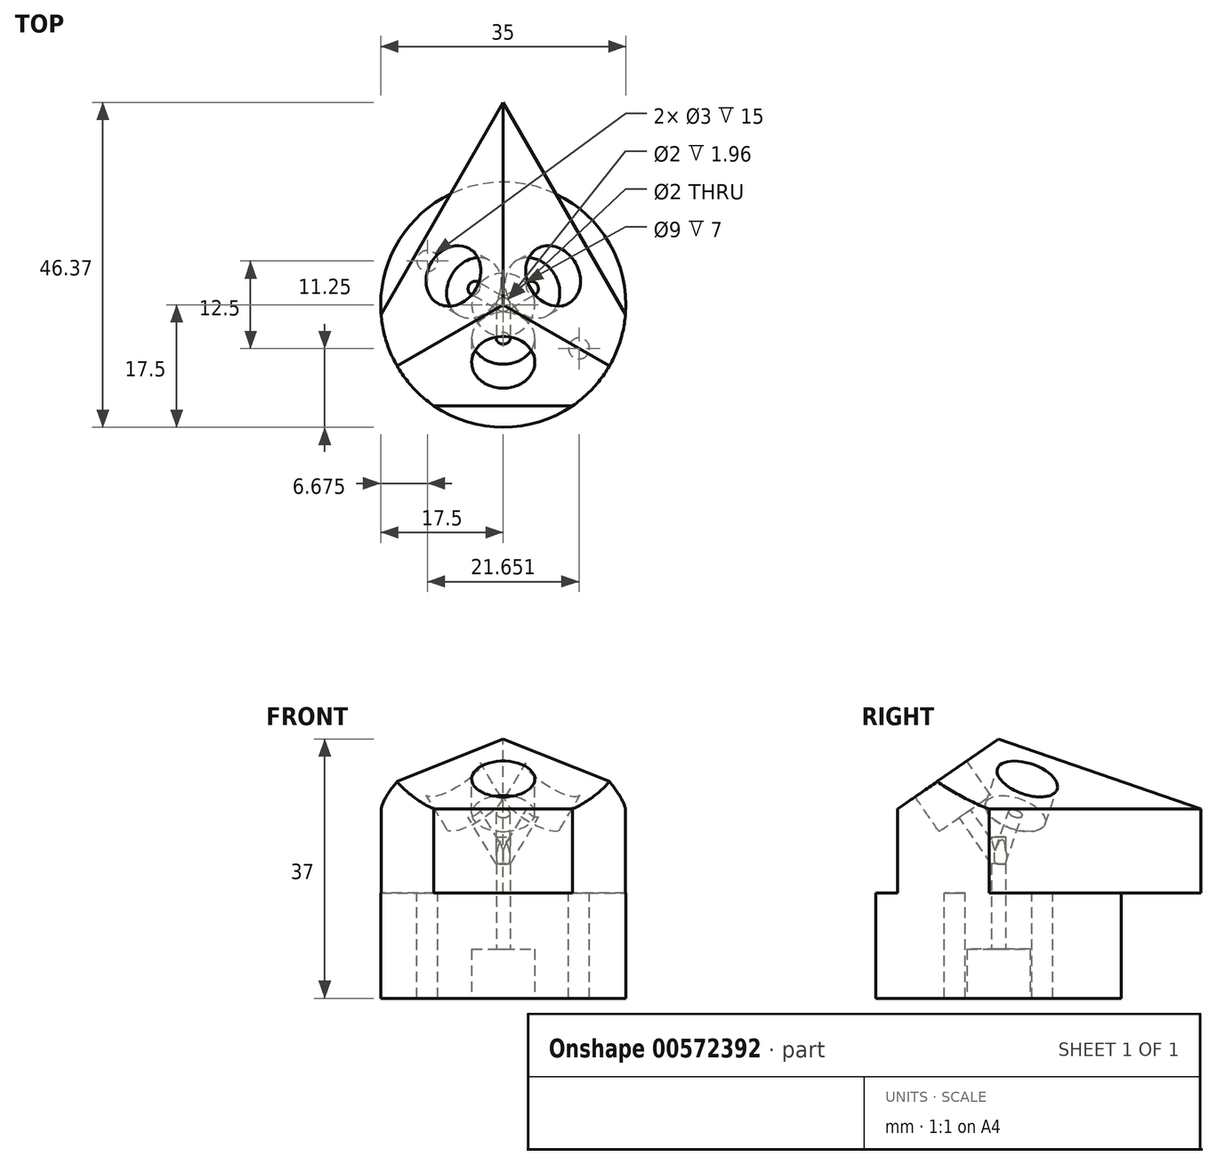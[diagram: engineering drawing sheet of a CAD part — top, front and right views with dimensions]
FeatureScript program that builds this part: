
annotation { "Feature Type Name" : "Feature", "Feature Type Description" : "" }
export const myFeature = defineFeature(function(context is Context, id is Id, definition is map)
    precondition{}
    {
        {
            assignVariable(context, id + "F0", {"name" : "BaseHeight", "anyValue" : 12});
        }
        {
            assignVariable(context, id + "F1", {"name" : "BarbDepth", "anyValue" : 6});
        }
        {
            var Q0;
            Q0=qCreatedBy(makeId("Top.planeOp"),FACE);
            var sketch = newSketch(context, id + "F2", { "sketchPlane" : qUnion([Q0])});
            skLineSegment(sketch, "E0", {"start": v(0, 28.87) * mm, "end": v(-25, -14.43) * mm});
            skLineSegment(sketch, "E1", {"start": v(-25, -14.43) * mm, "end": v(25, -14.43) * mm});
            skLineSegment(sketch, "E2", {"start": v(25, -14.43) * mm, "end": v(0, 28.87) * mm});
            skLineSegment(sketch, "E3", {"start": v(-12.5, 7.22) * mm, "end": v(0, 0) * mm, "construction": true});
            skLineSegment(sketch, "E4", {"start": v(0, 0) * mm, "end": v(0, -14.43) * mm, "construction": true});
            skLineSegment(sketch, "E5", {"start": v(0, 0) * mm, "end": v(12.5, 7.22) * mm, "construction": true});
            skSolve(sketch);
        }
        {
            var Q0;
            Q0=makeQuery(id+"F2.imprint","IMPRINT",FACE,{"disambiguationData":[TD([[makeQuery(id+"F2.imprint","IMPRINT",EDGE,{"derivedFrom":sQuery(id+"F2.wireOp",EDGE,"E0")}),1.0]])]});
            extrude(context, id + "F3", {"entities" : qUnion([Q0]), "oppositeDirection" : true, "depth" : (getVariable(context, 'BaseHeight')) * mm, "offsetDistance" : 25 * mm});
        }
        {
            var Q0;
            Q0=makeQuery(id+"F3.opExtrude","CAP_FACE",FACE,{"disambiguationData":[OSD([sQuery(id+"F2.wireOp",EDGE,"E0"),sQuery(id+"F2.wireOp",EDGE,"E1"),sQuery(id+"F2.wireOp",EDGE,"E2")])],"isStart":true});
            cPlane(context, id + "F4", {"entities" : qUnion([Q0]), "cplaneType" : CPlaneType.OFFSET, "offset" : 10 * mm, "width" : 150 * mm, "height" : 150 * mm});
        }
        {
            var Q0;
            Q0=qCreatedBy(id+"F4.planeOp",FACE);
            var sketch = newSketch(context, id + "F5", { "sketchPlane" : qUnion([Q0])});
            skPoint(sketch, "E6.0", {"position": v(0, 0) * mm});
            skSolve(sketch);
        }
        {
            var Q1;
            Q1=makeQuery(id+"F3.opExtrude","CAP_FACE",FACE,{"disambiguationData":[OSD([sQuery(id+"F2.wireOp",EDGE,"E0"),sQuery(id+"F2.wireOp",EDGE,"E1"),sQuery(id+"F2.wireOp",EDGE,"E2")])],"isStart":true});
            var Q2;
            Q2=sQuery(id+"F5.wireOp",VERTEX,"E6.0");
            loft(context, id + "F6", {"operationType" : NewBodyOperationType.ADD, "sheetProfilesArray" : [{ "sheetProfileEntities" : qUnion([Q1]) }, { "sheetProfileEntities" : qUnion([Q2]) }]});
        }
        {
            var Q0;
            Q0=makeQuery(id+"F3.opExtrude","CAP_FACE",FACE,{"disambiguationData":[OSD([sQuery(id+"F2.wireOp",EDGE,"E0"),sQuery(id+"F2.wireOp",EDGE,"E1"),sQuery(id+"F2.wireOp",EDGE,"E2")])],"isStart":false});
            var sketch = newSketch(context, id + "F7", { "sketchPlane" : qUnion([Q0])});
            skLineSegment(sketch, "E7", {"start": v(12.5, -7.22) * mm, "end": v(0, 0) * mm, "construction": true});
            skLineSegment(sketch, "E8", {"start": v(0, 0) * mm, "end": v(0, 14.43) * mm, "construction": true});
            skLineSegment(sketch, "E9", {"start": v(-12.5, -7.22) * mm, "end": v(0, 0) * mm, "construction": true});
            skSolve(sketch);
        }
        {
            var Q0;
            Q0=makeQuery(id+"F7.imprint","IMPRINT",FACE,{"disambiguationData":[TD([[makeQuery(id+"F7.imprint","IMPRINT",EDGE,{"derivedFrom":makeQuery(id+"F3.opExtrude","CAP_EDGE",EDGE,{"disambiguationData":[OSD([sQuery(id+"F2.wireOp",EDGE,"E0")])],"isStart":false})}),-1.0]])]});
            var sketch = newSketch(context, id + "F8", { "sketchPlane" : qUnion([Q0])});
            skCircle(sketch, "E10", {"center": v(0, 0) * mm, "radius": 1 * mm});
            skSolve(sketch);
        }
        {
            var Q0;
            Q0=makeQuery(id+"F8.imprint","IMPRINT",FACE,{"disambiguationData":[TD([[makeQuery(id+"F8.imprint","IMPRINT",EDGE,{"derivedFrom":sQuery(id+"F8.wireOp",EDGE,"E10")}),1.0]])]});
            extrude(context, id + "F9", {"entities" : qUnion([Q0]), "operationType" : NewBodyOperationType.REMOVE, "oppositeDirection" : true, "depth" : 8 * mm, "offsetDistance" : 25 * mm});
        }
        {
            var Q0;
            Q0=makeQuery(id+"F7.imprint","IMPRINT",FACE,{"disambiguationData":[TD([[makeQuery(id+"F7.imprint","IMPRINT",EDGE,{"derivedFrom":makeQuery(id+"F3.opExtrude","CAP_EDGE",EDGE,{"disambiguationData":[OSD([sQuery(id+"F2.wireOp",EDGE,"E0")])],"isStart":false})}),-1.0]])]});
            var sketch = newSketch(context, id + "F10", { "sketchPlane" : qUnion([Q0])});
            skCircle(sketch, "E11", {"center": v(0, 0) * mm, "radius": 4.5 * mm});
            skSolve(sketch);
        }
        {
            var Q0;
            Q0=makeQuery(id+"F10.imprint","IMPRINT",FACE,{"disambiguationData":[TD([[makeQuery(id+"F10.imprint","IMPRINT",EDGE,{"derivedFrom":sQuery(id+"F10.wireOp",EDGE,"E11")}),1.0]])]});
            extrude(context, id + "F11", {"entities" : qUnion([Q0]), "operationType" : NewBodyOperationType.REMOVE, "oppositeDirection" : true, "depth" : 2 * mm, "offsetDistance" : 25 * mm});
        }
        {
            var Q0;
            {var subQ0=sQuery(id+"F2.wireOp",EDGE,"E1");var subQ1=sQuery(id+"F2.wireOp",EDGE,"E2");var subQ2=sQuery(id+"F2.wireOp",EDGE,"E0");Q0=makeQuery(id+"F6.opLoft","SWEPT_FACE",FACE,{"disambiguationData":[OSD([subQ2,subQ0,subQ1]),TDD([makeQuery(id+"F3.opExtrude","CAP_VERTEX",VERTEX,{"disambiguationData":[OSD([subQ2,subQ0])],"isStart":true}),makeQuery(id+"F3.opExtrude","CAP_VERTEX",VERTEX,{"disambiguationData":[OSD([subQ0,subQ1])],"isStart":true}),makeQuery(id+"F3.opExtrude","CAP_EDGE",EDGE,{"disambiguationData":[OSD([subQ0])],"isStart":true})])]});}
            var sketch = newSketch(context, id + "F12", { "sketchPlane" : qUnion([Q0])});
            skPoint(sketch, "E12.endSnap0", {"position": v(0, -11.86) * mm});
            skLineSegment(sketch, "E13", {"start": v(-12.5, -3.08) * mm, "end": v(0, -4.3) * mm, "construction": true});
            skLineSegment(sketch, "E14", {"start": v(0, -4.3) * mm, "end": v(0, -11.86) * mm, "construction": true});
            skLineSegment(sketch, "E15", {"start": v(12.5, -3.08) * mm, "end": v(0, -4.3) * mm, "construction": true});
            skCircle(sketch, "E16", {"center": v(0, -4.3) * mm, "radius": 1 * mm});
            skCircle(sketch, "E17", {"center": v(0, -4.3) * mm, "radius": 4.5 * mm});
            skLineSegment(sketch, "E18", {"start": v(0, 5.7) * mm, "end": v(0, -4.3) * mm, "construction": true});
            skSolve(sketch);
        }
        {
            var Q0;
            Q0=makeQuery(id+"F12.imprint","IMPRINT",FACE,{"disambiguationData":[TD([[makeQuery(id+"F12.imprint","IMPRINT",EDGE,{"derivedFrom":sQuery(id+"F12.wireOp",EDGE,"E16")}),1.0]])]});
            var Q1;
            Q1=makeQuery(id+"F9.boolean.opBoolean","COPY",FACE,{"derivedFrom":makeQuery(id+"F9.opExtrude","SWEPT_FACE",FACE,{"disambiguationData":[OSD([sQuery(id+"F8.wireOp",EDGE,"E10")])]})});
            extrude(context, id + "F13", {"entities" : qUnion([Q0]), "operationType" : NewBodyOperationType.REMOVE, "endBound" : BoundingType.UP_TO_SURFACE, "oppositeDirection" : true, "depth" : 25 * mm, "endBoundEntityFace" : qUnion([Q1]), "offsetDistance" : 25 * mm});
        }
        {
            var Q0;
            Q0 = qSketchRegion(id + "F12", true);
            extrude(context, id + "F14", {"entities" : qUnion([Q0]), "operationType" : NewBodyOperationType.REMOVE, "oppositeDirection" : true, "depth" : (getVariable(context, 'BarbDepth')) * mm, "offsetDistance" : 25 * mm});
        }
        {
            var Q0;
            {var subQ0=sQuery(id+"F2.wireOp",EDGE,"E0");var subQ1=sQuery(id+"F2.wireOp",EDGE,"E1");var subQ2=sQuery(id+"F2.wireOp",EDGE,"E2");Q0=makeQuery(id+"F6.opLoft","SWEPT_FACE",FACE,{"disambiguationData":[OSD([subQ0,subQ1,subQ2]),TDD([makeQuery(id+"F3.opExtrude","CAP_VERTEX",VERTEX,{"disambiguationData":[OSD([subQ0,subQ2])],"isStart":true}),makeQuery(id+"F3.opExtrude","CAP_VERTEX",VERTEX,{"disambiguationData":[OSD([subQ0,subQ1])],"isStart":true}),makeQuery(id+"F3.opExtrude","CAP_EDGE",EDGE,{"disambiguationData":[OSD([subQ0])],"isStart":true})])]});}
            var sketch = newSketch(context, id + "F15", { "sketchPlane" : qUnion([Q0])});
            skLineSegment(sketch, "E19", {"start": v(-9.7, 6.82) * mm, "end": v(-3.52, 2.47) * mm, "construction": true});
            skCircle(sketch, "E20", {"center": v(-3.52, 2.47) * mm, "radius": 1 * mm});
            skCircle(sketch, "E21", {"center": v(-3.52, 2.47) * mm, "radius": 4.5 * mm});
            skLineSegment(sketch, "E22", {"start": v(-3.52, 2.47) * mm, "end": v(4.66, -3.27) * mm, "construction": true});
            skSolve(sketch);
        }
        {
            var Q0;
            Q0=makeQuery(id+"F15.imprint","IMPRINT",FACE,{"disambiguationData":[TD([[makeQuery(id+"F15.imprint","IMPRINT",EDGE,{"derivedFrom":sQuery(id+"F15.wireOp",EDGE,"E20")}),1.0]])]});
            var Q1;
            Q1=makeQuery(id+"F9.boolean.opBoolean","COPY",FACE,{"derivedFrom":makeQuery(id+"F9.opExtrude","SWEPT_FACE",FACE,{"disambiguationData":[OSD([sQuery(id+"F8.wireOp",EDGE,"E10")])]})});
            extrude(context, id + "F16", {"entities" : qUnion([Q0]), "operationType" : NewBodyOperationType.REMOVE, "endBound" : BoundingType.UP_TO_SURFACE, "oppositeDirection" : true, "depth" : 25 * mm, "endBoundEntityFace" : qUnion([Q1]), "offsetDistance" : 25 * mm});
        }
        {
            var Q0;
            Q0 = qSketchRegion(id + "F15", true);
            extrude(context, id + "F17", {"entities" : qUnion([Q0]), "operationType" : NewBodyOperationType.REMOVE, "oppositeDirection" : true, "depth" : (getVariable(context, 'BarbDepth')) * mm, "offsetDistance" : 25 * mm});
        }
        {
            var Q0;
            {var subQ0=sQuery(id+"F2.wireOp",EDGE,"E2");var subQ1=sQuery(id+"F2.wireOp",EDGE,"E1");var subQ2=sQuery(id+"F2.wireOp",EDGE,"E0");Q0=makeQuery(id+"F6.opLoft","SWEPT_FACE",FACE,{"disambiguationData":[OSD([subQ2,subQ1,subQ0]),TDD([makeQuery(id+"F3.opExtrude","CAP_VERTEX",VERTEX,{"disambiguationData":[OSD([subQ2,subQ0])],"isStart":true}),makeQuery(id+"F3.opExtrude","CAP_VERTEX",VERTEX,{"disambiguationData":[OSD([subQ1,subQ0])],"isStart":true}),makeQuery(id+"F3.opExtrude","CAP_EDGE",EDGE,{"disambiguationData":[OSD([subQ0])],"isStart":true})])]});}
            var sketch = newSketch(context, id + "F18", { "sketchPlane" : qUnion([Q0])});
            skLineSegment(sketch, "E23", {"start": v(9.7, 6.82) * mm, "end": v(3.52, 2.47) * mm, "construction": true});
            skCircle(sketch, "E24", {"center": v(3.52, 2.47) * mm, "radius": 1 * mm});
            skCircle(sketch, "E25", {"center": v(3.52, 2.47) * mm, "radius": 4.5 * mm});
            skLineSegment(sketch, "E26", {"start": v(3.52, 2.47) * mm, "end": v(-4.66, -3.27) * mm, "construction": true});
            skSolve(sketch);
        }
        {
            var Q0;
            Q0=makeQuery(id+"F18.imprint","IMPRINT",FACE,{"disambiguationData":[TD([[makeQuery(id+"F18.imprint","IMPRINT",EDGE,{"derivedFrom":sQuery(id+"F18.wireOp",EDGE,"E24")}),1.0]])]});
            var Q1;
            Q1=makeQuery(id+"F9.boolean.opBoolean","COPY",FACE,{"derivedFrom":makeQuery(id+"F9.opExtrude","SWEPT_FACE",FACE,{"disambiguationData":[OSD([sQuery(id+"F8.wireOp",EDGE,"E10")])]})});
            extrude(context, id + "F19", {"entities" : qUnion([Q0]), "operationType" : NewBodyOperationType.REMOVE, "endBound" : BoundingType.UP_TO_SURFACE, "oppositeDirection" : true, "depth" : 25 * mm, "endBoundEntityFace" : qUnion([Q1]), "offsetDistance" : 25 * mm});
        }
        {
            var Q0;
            Q0 = qSketchRegion(id + "F18", true);
            extrude(context, id + "F20", {"entities" : qUnion([Q0]), "operationType" : NewBodyOperationType.REMOVE, "oppositeDirection" : true, "depth" : (getVariable(context, 'BarbDepth')) * mm, "offsetDistance" : 25 * mm});
        }
        {
            var Q0;
            Q0=makeQuery(id+"F7.imprint","IMPRINT",FACE,{"disambiguationData":[TD([[makeQuery(id+"F7.imprint","IMPRINT",EDGE,{"derivedFrom":makeQuery(id+"F3.opExtrude","CAP_EDGE",EDGE,{"disambiguationData":[OSD([sQuery(id+"F2.wireOp",EDGE,"E0")])],"isStart":false})}),-1.0]])]});
            var sketch = newSketch(context, id + "F21", { "sketchPlane" : qUnion([Q0])});
            skCircle(sketch, "E27", {"center": v(0, 0) * mm, "radius": 17.5 * mm});
            skCircle(sketch, "E28", {"center": v(0, 0) * mm, "radius": 23.46 * mm});
            skSolve(sketch);
        }
        {
            var Q0;
            {var subQ0=sQuery(id+"F21.wireOp",EDGE,"E27");var subQ1=makeQuery(id+"F7.imprint","IMPRINT",EDGE,{"derivedFrom":makeQuery(id+"F3.opExtrude","CAP_EDGE",EDGE,{"disambiguationData":[OSD([sQuery(id+"F2.wireOp",EDGE,"E0")])],"isStart":false})});var subQ2=makeQuery(id+"F21.imprint","INTERSECT",VERTEX,{"disambiguationData":[OD(1.0)],"derivedFrom":[subQ1,subQ0]});Q0=makeQuery(id+"F21.imprint","IMPRINT",FACE,{"disambiguationData":[TD([[makeQuery(id+"F21.imprint","IMPRINT",EDGE,{"disambiguationData":[TD([[subQ2,-1.0]])],"derivedFrom":subQ0}),-1.0]])]});}
            var Q1;
            {var subQ0=sQuery(id+"F21.wireOp",EDGE,"E27");var subQ1=makeQuery(id+"F7.imprint","IMPRINT",EDGE,{"derivedFrom":makeQuery(id+"F3.opExtrude","CAP_EDGE",EDGE,{"disambiguationData":[OSD([sQuery(id+"F2.wireOp",EDGE,"E1")])],"isStart":false})});var subQ2=makeQuery(id+"F21.imprint","INTERSECT",VERTEX,{"disambiguationData":[OD(1.0)],"derivedFrom":[subQ1,subQ0]});Q1=makeQuery(id+"F21.imprint","IMPRINT",FACE,{"disambiguationData":[TD([[makeQuery(id+"F21.imprint","IMPRINT",EDGE,{"disambiguationData":[TD([[subQ2,1.0]])],"derivedFrom":subQ0}),-1.0]])]});}
            var Q2;
            {var subQ0=sQuery(id+"F21.wireOp",EDGE,"E27");var subQ1=makeQuery(id+"F7.imprint","IMPRINT",EDGE,{"derivedFrom":makeQuery(id+"F3.opExtrude","CAP_EDGE",EDGE,{"disambiguationData":[OSD([sQuery(id+"F2.wireOp",EDGE,"E1")])],"isStart":false})});var subQ2=makeQuery(id+"F21.imprint","INTERSECT",VERTEX,{"disambiguationData":[OD(0.0)],"derivedFrom":[subQ1,subQ0]});Q2=makeQuery(id+"F21.imprint","IMPRINT",FACE,{"disambiguationData":[TD([[makeQuery(id+"F21.imprint","IMPRINT",EDGE,{"disambiguationData":[TD([[subQ2,-1.0]])],"derivedFrom":subQ0}),-1.0]])]});}
            var Q3;
            {var subQ0=sQuery(id+"F21.wireOp",EDGE,"E27");var subQ1=makeQuery(id+"F7.imprint","IMPRINT",EDGE,{"derivedFrom":makeQuery(id+"F3.opExtrude","CAP_EDGE",EDGE,{"disambiguationData":[OSD([sQuery(id+"F2.wireOp",EDGE,"E1")])],"isStart":false})});var subQ2=makeQuery(id+"F21.imprint","INTERSECT",VERTEX,{"disambiguationData":[OD(1.0)],"derivedFrom":[subQ1,subQ0]});Q3=makeQuery(id+"F21.imprint","IMPRINT",FACE,{"disambiguationData":[TD([[makeQuery(id+"F21.imprint","IMPRINT",EDGE,{"disambiguationData":[TD([[subQ2,-1.0]])],"derivedFrom":subQ0}),-1.0]])]});}
            var Q4;
            {var subQ0=sQuery(id+"F21.wireOp",EDGE,"E27");var subQ1=makeQuery(id+"F7.imprint","IMPRINT",EDGE,{"derivedFrom":makeQuery(id+"F3.opExtrude","CAP_EDGE",EDGE,{"disambiguationData":[OSD([sQuery(id+"F2.wireOp",EDGE,"E1")])],"isStart":false})});var subQ2=makeQuery(id+"F21.imprint","INTERSECT",VERTEX,{"disambiguationData":[OD(0.0)],"derivedFrom":[subQ1,subQ0]});Q4=makeQuery(id+"F21.imprint","IMPRINT",FACE,{"disambiguationData":[TD([[makeQuery(id+"F21.imprint","IMPRINT",EDGE,{"disambiguationData":[TD([[subQ2,1.0]])],"derivedFrom":subQ0}),-1.0]])]});}
            var Q5;
            {var subQ0=sQuery(id+"F21.wireOp",EDGE,"E28");var subQ1=makeQuery(id+"F7.imprint","IMPRINT",EDGE,{"derivedFrom":makeQuery(id+"F3.opExtrude","CAP_EDGE",EDGE,{"disambiguationData":[OSD([sQuery(id+"F2.wireOp",EDGE,"E0")])],"isStart":false})});var subQ2=makeQuery(id+"F21.imprint","INTERSECT",VERTEX,{"disambiguationData":[OD(1.0)],"derivedFrom":[subQ1,subQ0]});Q5=makeQuery(id+"F21.imprint","IMPRINT",FACE,{"disambiguationData":[TD([[makeQuery(id+"F21.imprint","IMPRINT",EDGE,{"disambiguationData":[TD([[subQ2,-1.0]])],"derivedFrom":subQ0}),-1.0]])]});}
            var Q6;
            {var subQ0=sQuery(id+"F21.wireOp",EDGE,"E28");var subQ1=makeQuery(id+"F7.imprint","IMPRINT",EDGE,{"derivedFrom":makeQuery(id+"F3.opExtrude","CAP_EDGE",EDGE,{"disambiguationData":[OSD([sQuery(id+"F2.wireOp",EDGE,"E1")])],"isStart":false})});var subQ2=makeQuery(id+"F21.imprint","INTERSECT",VERTEX,{"disambiguationData":[OD(1.0)],"derivedFrom":[subQ1,subQ0]});Q6=makeQuery(id+"F21.imprint","IMPRINT",FACE,{"disambiguationData":[TD([[makeQuery(id+"F21.imprint","IMPRINT",EDGE,{"disambiguationData":[TD([[subQ2,-1.0]])],"derivedFrom":subQ0}),-1.0]])]});}
            var Q7;
            {var subQ0=sQuery(id+"F21.wireOp",EDGE,"E28");var subQ1=makeQuery(id+"F7.imprint","IMPRINT",EDGE,{"derivedFrom":makeQuery(id+"F3.opExtrude","CAP_EDGE",EDGE,{"disambiguationData":[OSD([sQuery(id+"F2.wireOp",EDGE,"E1")])],"isStart":false})});var subQ2=makeQuery(id+"F21.imprint","INTERSECT",VERTEX,{"disambiguationData":[OD(0.0)],"derivedFrom":[subQ1,subQ0]});Q7=makeQuery(id+"F21.imprint","IMPRINT",FACE,{"disambiguationData":[TD([[makeQuery(id+"F21.imprint","IMPRINT",EDGE,{"disambiguationData":[TD([[subQ2,1.0]])],"derivedFrom":subQ0}),-1.0]])]});}
            extrude(context, id + "F22", {"entities" : qUnion([Q0, Q1, Q2, Q3, Q4, Q5, Q6, Q7]), "operationType" : NewBodyOperationType.REMOVE, "oppositeDirection" : true, "depth" : 25 * mm, "offsetDistance" : 25 * mm});
        }
        {
            var Q0;
            Q0=makeQuery(id+"F3.opExtrude","CAP_FACE",FACE,{"disambiguationData":[OSD([sQuery(id+"F2.wireOp",EDGE,"E0"),sQuery(id+"F2.wireOp",EDGE,"E1"),sQuery(id+"F2.wireOp",EDGE,"E2")])],"isStart":false});
            var sketch = newSketch(context, id + "F23", { "sketchPlane" : qUnion([Q0])});
            skCircle(sketch, "E29", {"center": v(0, 0) * mm, "radius": 6.5 * mm});
            skLineSegment(sketch, "E30", {"start": v(15.16, 8.75) * mm, "end": v(-12.5, -7.22) * mm, "construction": true});
            skCircle(sketch, "E31", {"center": v(-10.83, -6.25) * mm, "radius": 1.5 * mm});
            skCircle(sketch, "E32", {"center": v(10.83, 6.25) * mm, "radius": 1.5 * mm});
            skCircle(sketch, "E33", {"center": v(0, 0) * mm, "radius": 12.5 * mm, "construction": true});
            skCircle(sketch, "E34", {"center": v(0, 0) * mm, "radius": 17.5 * mm});
            skSolve(sketch);
        }
        {
            var Q0;
            Q0 = qSketchRegion(id + "F23", true);
            var Q1;
            Q1=makeQuery(id+"F23.imprint","IMPRINT",FACE,{"disambiguationData":[TD([[makeQuery(id+"F23.imprint","IMPRINT",EDGE,{"derivedFrom":sQuery(id+"F23.wireOp",EDGE,"E29")}),1.0]])]});
            extrude(context, id + "F24", {"entities" : qUnion([Q0, Q1]), "operationType" : NewBodyOperationType.ADD, "depth" : 15 * mm, "offsetDistance" : 25 * mm});
        }
        {
            var Q0;
            Q0=makeQuery(id+"F11.boolean.opBoolean","COPY",FACE,{"derivedFrom":makeQuery(id+"F11.opExtrude","CAP_FACE",FACE,{"disambiguationData":[OSD([sQuery(id+"F10.wireOp",EDGE,"E11")])],"isStart":false})});
            extrude(context, id + "F25", {"entities" : qUnion([Q0]), "operationType" : NewBodyOperationType.ADD, "depth" : 10 * mm, "offsetDistance" : 25 * mm});
        }
    });
